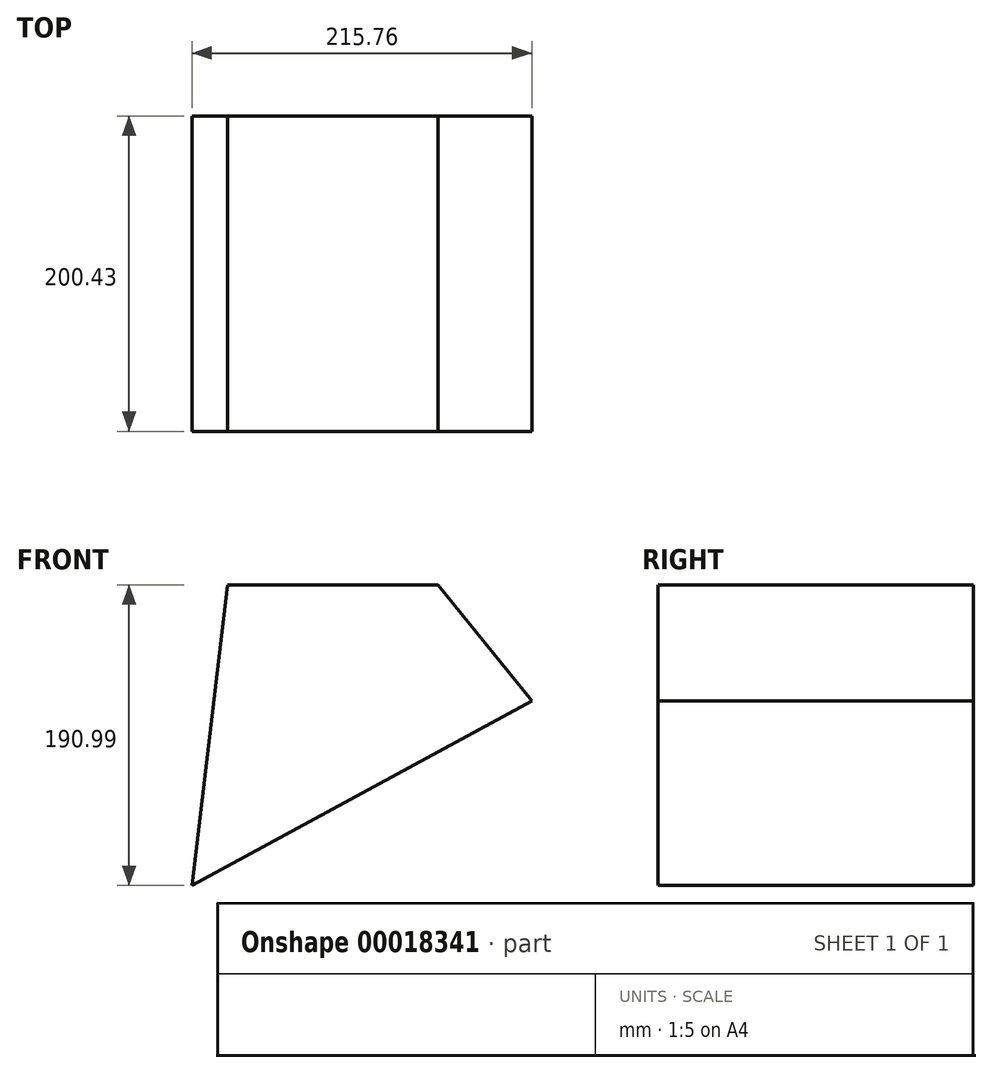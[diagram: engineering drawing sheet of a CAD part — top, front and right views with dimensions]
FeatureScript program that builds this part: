
annotation { "Feature Type Name" : "Feature", "Feature Type Description" : "" }
export const myFeature = defineFeature(function(context is Context, id is Id, definition is map)
    precondition{}
    {
        {
            var Q0;
            Q0=qCreatedBy(makeId("Front.planeOp"),FACE);
            var sketch = newSketch(context, id + "F0", { "sketchPlane" : qUnion([Q0])});
            skLineSegment(sketch, "E0", {"start": v(-187.01, 51.09) * mm, "end": v(-164.5, 242.08) * mm});
            skLineSegment(sketch, "E1", {"start": v(-164.5, 242.08) * mm, "end": v(-30.78, 242.08) * mm});
            skLineSegment(sketch, "E2", {"start": v(-30.78, 242.08) * mm, "end": v(28.75, 168.31) * mm});
            skLineSegment(sketch, "E3", {"start": v(28.75, 168.31) * mm, "end": v(-187.01, 51.09) * mm});
            skSolve(sketch);
        }
        {
            var Q0;
            Q0 = qSketchRegion(id + "F0", true);
            extrude(context, id + "F1", {"entities" : qUnion([Q0]), "depth" : 200.43 * mm});
        }
    });
